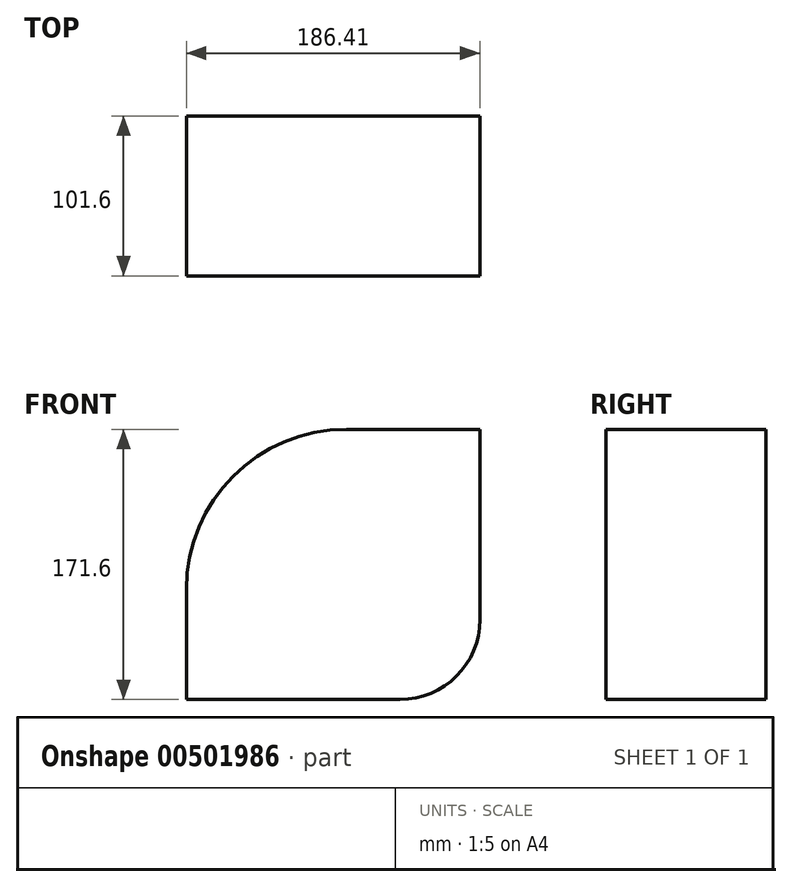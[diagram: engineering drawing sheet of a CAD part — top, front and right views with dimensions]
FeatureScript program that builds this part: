
annotation { "Feature Type Name" : "Feature", "Feature Type Description" : "" }
export const myFeature = defineFeature(function(context is Context, id is Id, definition is map)
    precondition{}
    {
        {
            var Q0;
            Q0=qCreatedBy(makeId("Front.planeOp"),FACE);
            var sketch = newSketch(context, id + "F0", { "sketchPlane" : qUnion([Q0])});
            skLineSegment(sketch, "E0.bottom", {"start": v(-16.44, 132.24) * mm, "end": v(68.37, 132.24) * mm});
            skLineSegment(sketch, "E0.top", {"start": v(-118.04, -39.36) * mm, "end": v(17.57, -39.36) * mm});
            skLineSegment(sketch, "E0.left", {"start": v(-118.04, 30.64) * mm, "end": v(-118.04, -39.36) * mm});
            skLineSegment(sketch, "E0.right", {"start": v(68.37, 132.24) * mm, "end": v(68.37, 11.44) * mm});
            skPoint(sketch, "E1.visualSharp", {"position": v(-118.04, 132.24) * mm});
            skArc(sketch, "E1.filletArc", {"start": v(-16.44, 132.24) * mm, "mid": v(-88.28, 102.48) * mm, "end": v(-118.04, 30.64) * mm});
            skPoint(sketch, "E2.visualSharp", {"position": v(68.37, -39.36) * mm});
            skArc(sketch, "E2.filletArc", {"start": v(17.57, -39.36) * mm, "mid": v(53.5, -24.48) * mm, "end": v(68.37, 11.44) * mm});
            skSolve(sketch);
        }
        {
            var Q0;
            Q0 = qSketchRegion(id + "F0", true);
            extrude(context, id + "F1", {"entities" : qUnion([Q0]), "depth" : 101.6 * mm});
        }
    });
